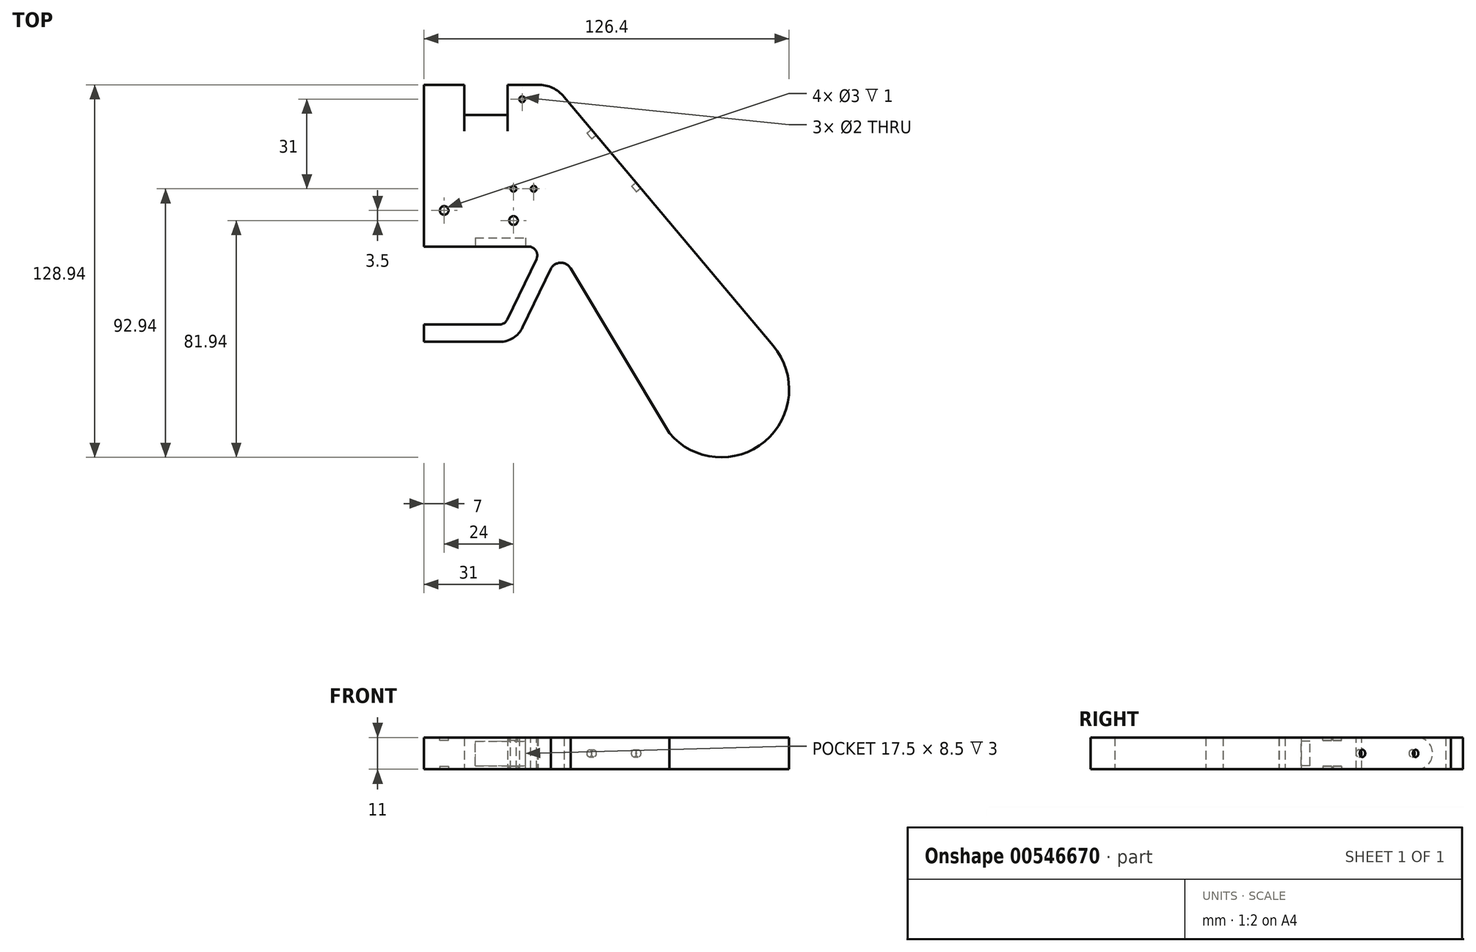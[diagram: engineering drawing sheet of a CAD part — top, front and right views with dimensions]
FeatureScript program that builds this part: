
annotation { "Feature Type Name" : "Feature", "Feature Type Description" : "" }
export const myFeature = defineFeature(function(context is Context, id is Id, definition is map)
    precondition{}
    {
        {
            var Q0;
            Q0=qCreatedBy(makeId("Top.planeOp"),FACE);
            var sketch = newSketch(context, id + "F0", { "sketchPlane" : qUnion([Q0])});
            skLineSegment(sketch, "E0", {"start": v(0, 0) * mm, "end": v(0, 56) * mm});
            skLineSegment(sketch, "E1", {"start": v(0, -27) * mm, "end": v(0, -33) * mm});
            skLineSegment(sketch, "E2", {"start": v(0, -33) * mm, "end": v(26.11, -33) * mm});
            skLineSegment(sketch, "E3", {"start": v(0, -27) * mm, "end": v(26.11, -27) * mm});
            skLineSegment(sketch, "E4", {"start": v(0, 56) * mm, "end": v(14, 56) * mm});
            skLineSegment(sketch, "E5", {"start": v(0, 0) * mm, "end": v(36.23, 0) * mm});
            skLineSegment(sketch, "E6", {"start": v(28.82, -25.3) * mm, "end": v(38.93, -4.3) * mm});
            skLineSegment(sketch, "E7.0", {"start": v(34.22, -27.9) * mm, "end": v(43.96, -7.7) * mm});
            skArc(sketch, "E8.filletArc", {"start": v(38.93, -4.3) * mm, "mid": v(38.77, -1.4) * mm, "end": v(36.23, 0) * mm});
            skArc(sketch, "E9.filletArc", {"start": v(26.11, -27) * mm, "mid": v(27.71, -26.54) * mm, "end": v(28.82, -25.3) * mm});
            skArc(sketch, "E10.0", {"start": v(26.11, -33) * mm, "mid": v(30.9, -31.62) * mm, "end": v(34.22, -27.9) * mm});
            skLineSegment(sketch, "E11.0", {"start": v(14, 40) * mm, "end": v(14, 56) * mm});
            skLineSegment(sketch, "E12.0", {"start": v(29, 40) * mm, "end": v(29, 56) * mm});
            skLineSegment(sketch, "E13.0", {"start": v(14, 40) * mm, "end": v(29, 40) * mm});
            skLineSegment(sketch, "E14.trimOffspring", {"start": v(29, 56) * mm, "end": v(39.5, 56) * mm});
            skLineSegment(sketch, "E15", {"start": v(48.5, 51.83) * mm, "end": v(120.9, -34.35) * mm});
            skLineSegment(sketch, "E16", {"start": v(84.94, -64.56) * mm, "end": v(50.76, -7.6) * mm});
            skArc(sketch, "E17", {"start": v(84.94, -64.56) * mm, "mid": v(118.02, -67.44) * mm, "end": v(120.9, -34.35) * mm});
            skArc(sketch, "E18", {"start": v(48.5, 51.83) * mm, "mid": v(44.49, 54.96) * mm, "end": v(39.5, 56) * mm});
            skPoint(sketch, "E19.orphan", {"position": v(46.5, 54.22) * mm});
            skCircle(sketch, "E20", {"center": v(34, 51) * mm, "radius": 1 * mm});
            skArc(sketch, "E21", {"start": v(50.76, -7.6) * mm, "mid": v(47.33, -5.6) * mm, "end": v(43.96, -7.7) * mm});
            skSolve(sketch);
        }
        {
            var Q0;
            Q0=qSketchRegion(id+"F0",true);
            extrude(context, id + "F1", {"entities" : qUnion([Q0]), "endBound" : BoundingType.SYMMETRIC, "depth" : 11 * mm});
        }
        {
            var Q0;
            Q0=makeQuery(id+"F1.opExtrude","SWEPT_FACE",FACE,{"disambiguationData":[OSD([sQuery(id+"F0.wireOp",EDGE,"E12.0")])]});
            var sketch = newSketch(context, id + "F2", { "sketchPlane" : qUnion([Q0])});
            skLineSegment(sketch, "E22", {"start": v(-40, -5.5) * mm, "end": v(-40, 5.5) * mm});
            skArc(sketch, "E23", {"start": v(-40, 5.5) * mm, "mid": v(-45.5, 0) * mm, "end": v(-40, -5.5) * mm});
            skSolve(sketch);
        }
        {
            var Q0;
            Q0=qSketchRegion(id+"F2",true);
            extrude(context, id + "F3", {"entities" : qUnion([Q0]), "operationType" : NewBodyOperationType.ADD, "depth" : 25 * mm});
        }
        {
            var Q0;
            Q0=makeQuery(id+"F1.opExtrude","CAP_FACE",FACE,{"disambiguationData":[OSD([sQuery(id+"F0.wireOp",EDGE,"E0"),sQuery(id+"F0.wireOp",EDGE,"E1"),sQuery(id+"F0.wireOp",EDGE,"E2"),sQuery(id+"F0.wireOp",EDGE,"E3"),sQuery(id+"F0.wireOp",EDGE,"E4"),sQuery(id+"F0.wireOp",EDGE,"E5"),sQuery(id+"F0.wireOp",EDGE,"E6"),sQuery(id+"F0.wireOp",EDGE,"E7.0"),sQuery(id+"F0.wireOp",EDGE,"E8.filletArc"),sQuery(id+"F0.wireOp",EDGE,"E9.filletArc"),sQuery(id+"F0.wireOp",EDGE,"E10.0"),sQuery(id+"F0.wireOp",EDGE,"E11.0"),sQuery(id+"F0.wireOp",EDGE,"E12.0"),sQuery(id+"F0.wireOp",EDGE,"E13.0"),sQuery(id+"F0.wireOp",EDGE,"E14.trimOffspring"),sQuery(id+"F0.wireOp",EDGE,"E15"),sQuery(id+"F0.wireOp",EDGE,"E16"),sQuery(id+"F0.wireOp",EDGE,"3d227ca1-747b-497a-97d5-58212d2cf885.filletArc"),sQuery(id+"F0.wireOp",EDGE,"E17"),sQuery(id+"F0.wireOp",EDGE,"E18"),sQuery(id+"F0.wireOp",EDGE,"E20")])],"isStart":false});
            var sketch = newSketch(context, id + "F4", { "sketchPlane" : qUnion([Q0])});
            skLineSegment(sketch, "E24", {"start": v(0, 56) * mm, "end": v(60.5, 56) * mm, "construction": true});
            skPoint(sketch, "E24.endSnap0", {"position": v(34.25, 56) * mm});
            skLineSegment(sketch, "E25", {"start": v(0, 56) * mm, "end": v(0, -13.4) * mm, "construction": true});
            skCircle(sketch, "E26", {"center": v(31, 20) * mm, "radius": 1 * mm});
            skCircle(sketch, "E27", {"center": v(38, 20) * mm, "radius": 1 * mm});
            skSolve(sketch);
        }
        {
            var Q0;
            Q0=qSketchRegion(id+"F4",true);
            extrude(context, id + "F5", {"entities" : qUnion([Q0]), "operationType" : NewBodyOperationType.REMOVE, "endBound" : BoundingType.THROUGH_ALL, "oppositeDirection" : true, "depth" : 25 * mm});
        }
        {
            var Q0;
            Q0=makeQuery(id+"F1.opExtrude","SWEPT_FACE",FACE,{"disambiguationData":[OSD([sQuery(id+"F0.wireOp",EDGE,"E5")])]});
            var sketch = newSketch(context, id + "F6", { "sketchPlane" : qUnion([Q0])});
            skLineSegment(sketch, "E28", {"start": v(35.23, -4.25) * mm, "end": v(35.23, 4.25) * mm});
            skLineSegment(sketch, "E29.0", {"start": v(17.73, -4.25) * mm, "end": v(17.73, 4.25) * mm});
            skLineSegment(sketch, "E30.0", {"start": v(17.73, 4.25) * mm, "end": v(35.23, 4.25) * mm});
            skLineSegment(sketch, "E31.MirrorCS", {"start": v(17.73, -4.25) * mm, "end": v(35.23, -4.25) * mm});
            skSolve(sketch);
        }
        {
            var Q0;
            Q0=qSketchRegion(id+"F6",true);
            extrude(context, id + "F7", {"entities" : qUnion([Q0]), "operationType" : NewBodyOperationType.REMOVE, "oppositeDirection" : true, "depth" : 3 * mm});
        }
        {
            var Q0;
            Q0=makeQuery(id+"F1.opExtrude","SWEPT_FACE",FACE,{"disambiguationData":[OSD([sQuery(id+"F0.wireOp",EDGE,"E15")])]});
            var sketch = newSketch(context, id + "F8", { "sketchPlane" : qUnion([Q0])});
            skCircle(sketch, "E32", {"center": v(-31.5, 0) * mm, "radius": 1.25 * mm});
            skCircle(sketch, "E33", {"center": v(-7.5, 0) * mm, "radius": 1.25 * mm});
            skSolve(sketch);
        }
        {
            var Q0;
            Q0=qSketchRegion(id+"F8",true);
            extrude(context, id + "F9", {"entities" : qUnion([Q0]), "operationType" : NewBodyOperationType.REMOVE, "oppositeDirection" : true, "depth" : 2 * mm});
        }
        {
            var Q0;
            Q0=makeQuery(id+"F1.opExtrude","CAP_FACE",FACE,{"disambiguationData":[OSD([sQuery(id+"F0.wireOp",EDGE,"E0"),sQuery(id+"F0.wireOp",EDGE,"E1"),sQuery(id+"F0.wireOp",EDGE,"E2"),sQuery(id+"F0.wireOp",EDGE,"E3"),sQuery(id+"F0.wireOp",EDGE,"E4"),sQuery(id+"F0.wireOp",EDGE,"E5"),sQuery(id+"F0.wireOp",EDGE,"E6"),sQuery(id+"F0.wireOp",EDGE,"E7.0"),sQuery(id+"F0.wireOp",EDGE,"E8.filletArc"),sQuery(id+"F0.wireOp",EDGE,"E9.filletArc"),sQuery(id+"F0.wireOp",EDGE,"E10.0"),sQuery(id+"F0.wireOp",EDGE,"E11.0"),sQuery(id+"F0.wireOp",EDGE,"E12.0"),sQuery(id+"F0.wireOp",EDGE,"E13.0"),sQuery(id+"F0.wireOp",EDGE,"E14.trimOffspring"),sQuery(id+"F0.wireOp",EDGE,"E15"),sQuery(id+"F0.wireOp",EDGE,"E16"),sQuery(id+"F0.wireOp",EDGE,"E17"),sQuery(id+"F0.wireOp",EDGE,"E18"),sQuery(id+"F0.wireOp",EDGE,"E20"),sQuery(id+"F0.wireOp",EDGE,"E21")])],"isStart":false});
            var sketch = newSketch(context, id + "F10", { "sketchPlane" : qUnion([Q0])});
            skLineSegment(sketch, "E34", {"start": v(7, 86.3) * mm, "end": v(7, -32.77) * mm, "construction": true});
            skLineSegment(sketch, "E35", {"start": v(31, 65.41) * mm, "end": v(31, -4.92) * mm, "construction": true});
            skLineSegment(sketch, "E36.0", {"start": v(0, 9) * mm, "end": v(36.23, 9) * mm, "construction": true});
            skLineSegment(sketch, "E37.0", {"start": v(0, 12.5) * mm, "end": v(36.23, 12.5) * mm, "construction": true});
            skCircle(sketch, "E38", {"center": v(7, 12.5) * mm, "radius": 1.5 * mm});
            skCircle(sketch, "E39", {"center": v(31, 9) * mm, "radius": 1.5 * mm});
            skSolve(sketch);
        }
        {
            var Q0;
            Q0=qSketchRegion(id+"F10",true);
            extrude(context, id + "F11", {"entities" : qUnion([Q0]), "operationType" : NewBodyOperationType.REMOVE, "oppositeDirection" : true, "depth" : 1 * mm});
        }
        {
            var Q0;
            Q0=makeQuery(id+"F1.opExtrude","CAP_FACE",FACE,{"disambiguationData":[OSD([sQuery(id+"F0.wireOp",EDGE,"E0"),sQuery(id+"F0.wireOp",EDGE,"E1"),sQuery(id+"F0.wireOp",EDGE,"E2"),sQuery(id+"F0.wireOp",EDGE,"E3"),sQuery(id+"F0.wireOp",EDGE,"E4"),sQuery(id+"F0.wireOp",EDGE,"E5"),sQuery(id+"F0.wireOp",EDGE,"E6"),sQuery(id+"F0.wireOp",EDGE,"E7.0"),sQuery(id+"F0.wireOp",EDGE,"E8.filletArc"),sQuery(id+"F0.wireOp",EDGE,"E9.filletArc"),sQuery(id+"F0.wireOp",EDGE,"E10.0"),sQuery(id+"F0.wireOp",EDGE,"E11.0"),sQuery(id+"F0.wireOp",EDGE,"E12.0"),sQuery(id+"F0.wireOp",EDGE,"E13.0"),sQuery(id+"F0.wireOp",EDGE,"E14.trimOffspring"),sQuery(id+"F0.wireOp",EDGE,"E15"),sQuery(id+"F0.wireOp",EDGE,"E16"),sQuery(id+"F0.wireOp",EDGE,"E17"),sQuery(id+"F0.wireOp",EDGE,"E18"),sQuery(id+"F0.wireOp",EDGE,"E20"),sQuery(id+"F0.wireOp",EDGE,"E21")])],"isStart":true});
            var sketch = newSketch(context, id + "F12", { "sketchPlane" : qUnion([Q0])});
            skCircle(sketch, "E40.0", {"center": v(7, -12.5) * mm, "radius": 1.5 * mm});
            skCircle(sketch, "E41.0", {"center": v(31, -9) * mm, "radius": 1.5 * mm});
            skSolve(sketch);
        }
        {
            var Q0;
            Q0=qSketchRegion(id+"F12",true);
            extrude(context, id + "F13", {"entities" : qUnion([Q0]), "operationType" : NewBodyOperationType.REMOVE, "oppositeDirection" : true, "depth" : 1 * mm});
        }
    });
